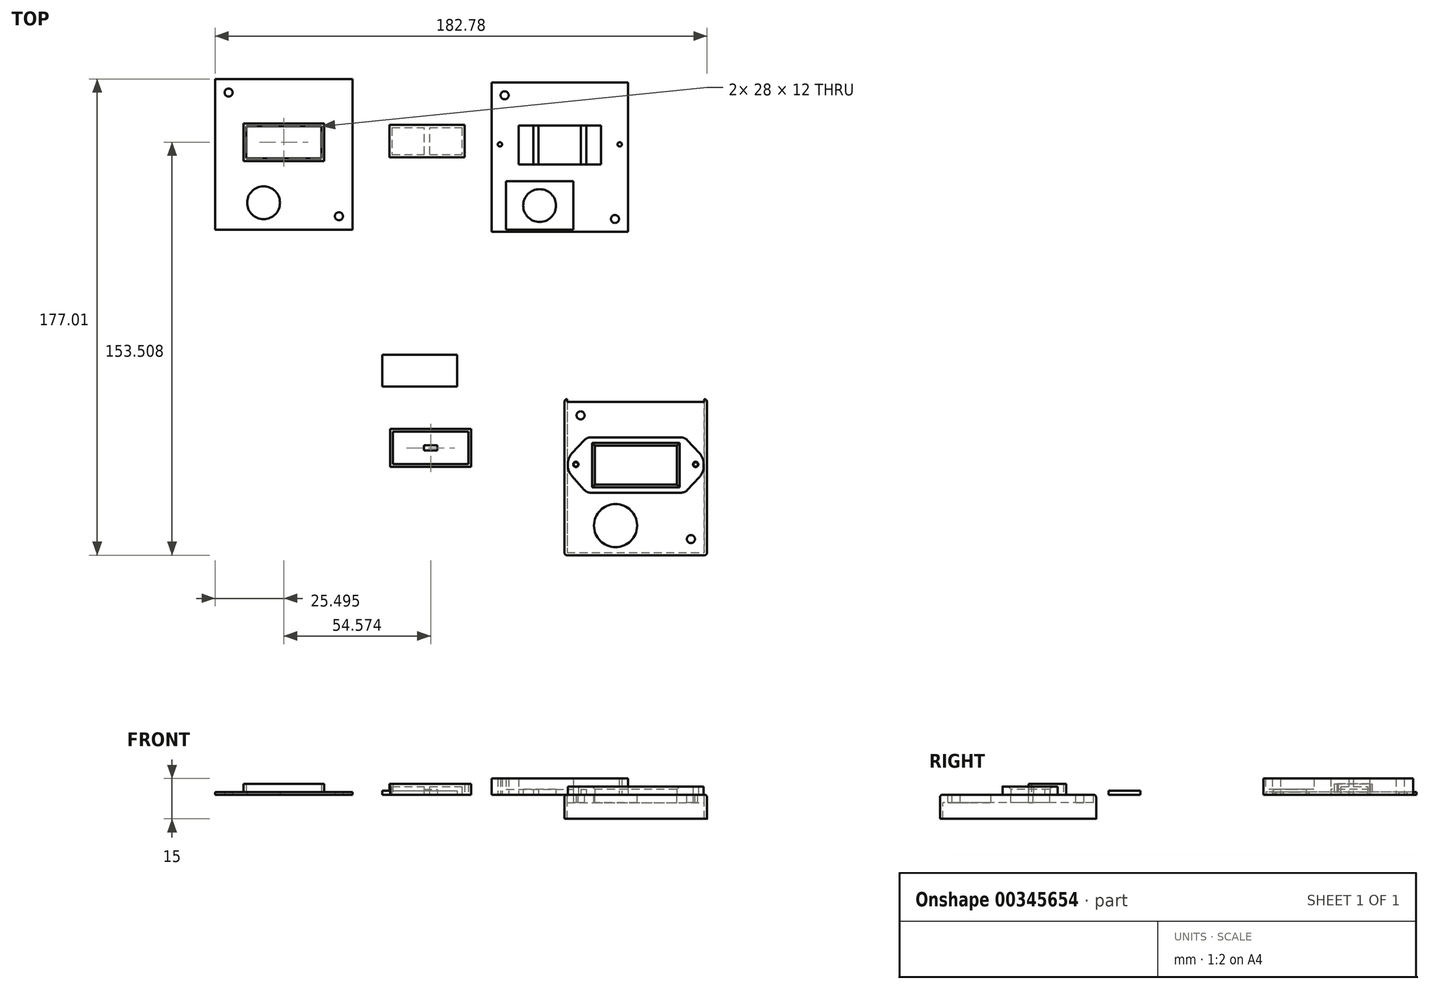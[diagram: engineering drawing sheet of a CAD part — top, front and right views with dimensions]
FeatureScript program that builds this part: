
annotation { "Feature Type Name" : "Feature", "Feature Type Description" : "" }
export const myFeature = defineFeature(function(context is Context, id is Id, definition is map)
    precondition{}
    {
        {
            var Q0;
            Q0=qCreatedBy(makeId("Top.planeOp"),FACE);
            var sketch = newSketch(context, id + "F0", { "sketchPlane" : qUnion([Q0])});
            skLineSegment(sketch, "E0.bottom", {"start": v(25.5, 28) * mm, "end": v(-25.5, 28) * mm});
            skLineSegment(sketch, "E0.top", {"start": v(25.5, -28) * mm, "end": v(-25.5, -28) * mm});
            skLineSegment(sketch, "E0.left", {"start": v(25.5, 28) * mm, "end": v(25.5, -28) * mm});
            skLineSegment(sketch, "E0.right", {"start": v(-25.5, 28) * mm, "end": v(-25.5, -28) * mm});
            skCircle(sketch, "E1", {"center": v(-20.5, 23) * mm, "radius": 1.5 * mm});
            skCircle(sketch, "E2", {"center": v(20.5, -23) * mm, "radius": 1.5 * mm});
            skCircle(sketch, "E3", {"center": v(-7.5, -18) * mm, "radius": 6.1 * mm});
            skLineSegment(sketch, "E4.bottom", {"start": v(-15.25, 11.75) * mm, "end": v(15.25, 11.75) * mm});
            skLineSegment(sketch, "E4.top", {"start": v(-15.25, -2.75) * mm, "end": v(15.25, -2.75) * mm});
            skLineSegment(sketch, "E4.left", {"start": v(-15.25, 11.75) * mm, "end": v(-15.25, -2.75) * mm});
            skLineSegment(sketch, "E4.right", {"start": v(15.25, 11.75) * mm, "end": v(15.25, -2.75) * mm});
            skPoint(sketch, "E5.middle", {"position": v(-103.8, -4.8) * mm});
            skLineSegment(sketch, "E6.bottom", {"start": v(-116.57, 11.54) * mm, "end": v(-88.57, 11.54) * mm});
            skLineSegment(sketch, "E6.top", {"start": v(-116.57, -0.46) * mm, "end": v(-88.57, -0.46) * mm});
            skLineSegment(sketch, "E6.left", {"start": v(-116.57, 11.54) * mm, "end": v(-116.57, -0.46) * mm});
            skLineSegment(sketch, "E6.right", {"start": v(-88.57, 11.54) * mm, "end": v(-88.57, -0.46) * mm});
            skLineSegment(sketch, "E7.bottom", {"start": v(-112.82, 11.54) * mm, "end": v(-110.32, 11.54) * mm});
            skLineSegment(sketch, "E7.top", {"start": v(-112.82, -0.46) * mm, "end": v(-110.32, -0.46) * mm});
            skLineSegment(sketch, "E7.left", {"start": v(-112.82, 11.54) * mm, "end": v(-112.82, -0.46) * mm});
            skLineSegment(sketch, "E7.right", {"start": v(-110.32, 11.54) * mm, "end": v(-110.32, -0.46) * mm});
            skLineSegment(sketch, "E8.bottom", {"start": v(-94.82, 11.54) * mm, "end": v(-92.32, 11.54) * mm});
            skLineSegment(sketch, "E8.top", {"start": v(-94.82, -0.46) * mm, "end": v(-92.32, -0.46) * mm});
            skLineSegment(sketch, "E8.left", {"start": v(-94.82, 11.54) * mm, "end": v(-94.82, -0.46) * mm});
            skLineSegment(sketch, "E8.right", {"start": v(-92.32, 11.54) * mm, "end": v(-92.32, -0.46) * mm});
            skLineSegment(sketch, "E9.bottom", {"start": v(-114.57, 8.54) * mm, "end": v(-108.57, 8.54) * mm, "construction": true});
            skLineSegment(sketch, "E9.top", {"start": v(-114.57, 2.54) * mm, "end": v(-108.57, 2.54) * mm, "construction": true});
            skLineSegment(sketch, "E9.left", {"start": v(-114.57, 8.54) * mm, "end": v(-114.57, 2.54) * mm, "construction": true});
            skLineSegment(sketch, "E9.right", {"start": v(-108.57, 8.54) * mm, "end": v(-108.57, 2.54) * mm, "construction": true});
            skLineSegment(sketch, "E10.bottom", {"start": v(-96.57, 8.54) * mm, "end": v(-90.57, 8.54) * mm, "construction": true});
            skLineSegment(sketch, "E10.top", {"start": v(-96.57, 2.54) * mm, "end": v(-90.57, 2.54) * mm, "construction": true});
            skLineSegment(sketch, "E10.left", {"start": v(-96.57, 8.54) * mm, "end": v(-96.57, 2.54) * mm, "construction": true});
            skLineSegment(sketch, "E10.right", {"start": v(-90.57, 8.54) * mm, "end": v(-90.57, 2.54) * mm, "construction": true});
            skLineSegment(sketch, "E11.bottom", {"start": v(-2.5, 11.75) * mm, "end": v(2.5, 11.75) * mm});
            skLineSegment(sketch, "E11.top", {"start": v(-2.5, -2.75) * mm, "end": v(2.5, -2.75) * mm});
            skLineSegment(sketch, "E11.left", {"start": v(-2.5, 11.75) * mm, "end": v(-2.5, -2.75) * mm});
            skLineSegment(sketch, "E11.right", {"start": v(2.5, 11.75) * mm, "end": v(2.5, -2.75) * mm});
            skLineSegment(sketch, "E12.bottom", {"start": v(-6.25, 10.5) * mm, "end": v(5.75, 10.5) * mm, "construction": true});
            skLineSegment(sketch, "E12.top", {"start": v(-6.25, -1.5) * mm, "end": v(5.75, -1.5) * mm, "construction": true});
            skLineSegment(sketch, "E12.left", {"start": v(-6.25, 10.5) * mm, "end": v(-6.25, -1.5) * mm, "construction": true});
            skLineSegment(sketch, "E12.right", {"start": v(5.75, 10.5) * mm, "end": v(5.75, -1.5) * mm, "construction": true});
            skLineSegment(sketch, "E13.bottom", {"start": v(-128.07, 29.04) * mm, "end": v(-77.07, 29.04) * mm});
            skLineSegment(sketch, "E13.top", {"start": v(-128.07, -26.96) * mm, "end": v(-77.07, -26.96) * mm});
            skLineSegment(sketch, "E13.left", {"start": v(-128.07, 29.04) * mm, "end": v(-128.07, -26.96) * mm});
            skLineSegment(sketch, "E13.right", {"start": v(-77.07, 29.04) * mm, "end": v(-77.07, -26.96) * mm});
            skCircle(sketch, "E14", {"center": v(-123.07, 24.04) * mm, "radius": 1.5 * mm});
            skCircle(sketch, "E15", {"center": v(-82.07, -21.96) * mm, "radius": 1.5 * mm});
            skLineSegment(sketch, "E16.bottom", {"start": v(-14, 10.5) * mm, "end": v(14, 10.5) * mm, "construction": true});
            skLineSegment(sketch, "E16.top", {"start": v(-14, -1.5) * mm, "end": v(14, -1.5) * mm, "construction": true});
            skLineSegment(sketch, "E16.left", {"start": v(-14, 10.5) * mm, "end": v(-14, -1.5) * mm, "construction": true});
            skLineSegment(sketch, "E16.right", {"start": v(14, 10.5) * mm, "end": v(14, -1.5) * mm, "construction": true});
            skCircle(sketch, "E17", {"center": v(-110.07, -16.96) * mm, "radius": 6.1 * mm});
            skSolve(sketch);
        }
        {
            var Q0;
            Q0=makeQuery(id+"F0.imprint","IMPRINT",FACE,{"disambiguationData":[TD([[makeQuery(id+"F0.imprint","IMPRINT",EDGE,{"derivedFrom":sQuery(id+"F0.wireOp",EDGE,"E0.bottom")}),1.0]])]});
            var Q1;
            Q1=makeQuery(id+"F0.imprint","IMPRINT",FACE,{"disambiguationData":[TD([[makeQuery(id+"F0.imprint","IMPRINT",EDGE,{"derivedFrom":sQuery(id+"F0.wireOp",EDGE,"LN2d2Qam-zQ4N-hJWI-jsZm-hQ2YjQqxJFMe.bottom")}),-1.0]])]});
            var Q2;
            Q2=makeQuery(id+"F0.imprint","IMPRINT",FACE,{"disambiguationData":[TD([[makeQuery(id+"F0.imprint","IMPRINT",EDGE,{"derivedFrom":sQuery(id+"F0.wireOp",EDGE,"Tyq8l7xN-NJ6r-rAiC-5Q4v-MCzvgNdMf9WX.bottom")}),-1.0]])]});
            var Q3;
            Q3=makeQuery(id+"F0.imprint","IMPRINT",FACE,{"disambiguationData":[TD([[makeQuery(id+"F0.imprint","IMPRINT",EDGE,{"derivedFrom":sQuery(id+"F0.wireOp",EDGE,"E11.bottom")}),-1.0]])]});
            var Q4;
            {var subQ12=sQuery(id+"F0.wireOp",EDGE,"E6.left");Q4=makeQuery(id+"F0.imprint","IMPRINT",FACE,{"disambiguationData":[TD([[makeQuery(id+"F0.imprint","IMPRINT",EDGE,{"derivedFrom":subQ12}),-1.0]])]});}
            var Q5;
            Q5=makeQuery(id+"F0.imprint","IMPRINT",FACE,{"disambiguationData":[TD([[makeQuery(id+"F0.imprint","IMPRINT",EDGE,{"derivedFrom":sQuery(id+"F0.wireOp",EDGE,"E7.bottom")}),-1.0]])]});
            var Q6;
            Q6=makeQuery(id+"F0.imprint","IMPRINT",FACE,{"disambiguationData":[TD([[makeQuery(id+"F0.imprint","IMPRINT",EDGE,{"derivedFrom":sQuery(id+"F0.wireOp",EDGE,"E8.bottom")}),-1.0]])]});
            var Q7;
            Q7=makeQuery(id+"F0.imprint","IMPRINT",FACE,{"disambiguationData":[TD([[makeQuery(id+"F0.imprint","IMPRINT",EDGE,{"derivedFrom":sQuery(id+"F0.wireOp",EDGE,"V3zyF6Pa-9TGi-MSfi-dUwD-Oto6uP0OLka4.bottom")}),-1.0]])]});
            extrude(context, id + "F1", {"entities" : qUnion([Q0, Q1, Q2, Q3, Q4, Q5, Q6, Q7]), "depth" : 1 * mm});
        }
        {
            var Q0;
            Q0=qCreatedBy(makeId("Top.planeOp"),FACE);
            var sketch = newSketch(context, id + "F2", { "sketchPlane" : qUnion([Q0])});
            skPoint(sketch, "E18.middle", {"position": v(28.78, -122.02) * mm});
            skLineSegment(sketch, "E19.bottom", {"start": v(14.21, -108.47) * mm, "end": v(42.21, -108.47) * mm, "construction": true});
            skLineSegment(sketch, "E19.top", {"start": v(14.21, -120.47) * mm, "end": v(42.21, -120.47) * mm, "construction": true});
            skLineSegment(sketch, "E19.left", {"start": v(14.21, -108.47) * mm, "end": v(14.21, -120.47) * mm, "construction": true});
            skLineSegment(sketch, "E19.right", {"start": v(42.21, -108.47) * mm, "end": v(42.21, -120.47) * mm, "construction": true});
            skLineSegment(sketch, "E20.bottom", {"start": v(20.96, -108.47) * mm, "end": v(23.46, -108.47) * mm, "construction": true});
            skLineSegment(sketch, "E20.top", {"start": v(20.96, -120.47) * mm, "end": v(23.46, -120.47) * mm, "construction": true});
            skLineSegment(sketch, "E20.left", {"start": v(20.96, -108.47) * mm, "end": v(20.96, -120.47) * mm, "construction": true});
            skLineSegment(sketch, "E20.right", {"start": v(23.46, -108.47) * mm, "end": v(23.46, -120.47) * mm, "construction": true});
            skLineSegment(sketch, "E21.bottom", {"start": v(32.96, -108.47) * mm, "end": v(35.46, -108.47) * mm, "construction": true});
            skLineSegment(sketch, "E21.top", {"start": v(32.96, -120.47) * mm, "end": v(35.46, -120.47) * mm, "construction": true});
            skLineSegment(sketch, "E21.left", {"start": v(32.96, -108.47) * mm, "end": v(32.96, -120.47) * mm, "construction": true});
            skLineSegment(sketch, "E21.right", {"start": v(35.46, -108.47) * mm, "end": v(35.46, -120.47) * mm, "construction": true});
            skLineSegment(sketch, "E22.bottom", {"start": v(19.21, -111.47) * mm, "end": v(25.21, -111.47) * mm, "construction": true});
            skLineSegment(sketch, "E22.top", {"start": v(19.21, -117.47) * mm, "end": v(25.21, -117.47) * mm, "construction": true});
            skLineSegment(sketch, "E22.left", {"start": v(19.21, -111.47) * mm, "end": v(19.21, -117.47) * mm, "construction": true});
            skLineSegment(sketch, "E22.right", {"start": v(25.21, -111.47) * mm, "end": v(25.21, -117.47) * mm, "construction": true});
            skLineSegment(sketch, "E23.bottom", {"start": v(31.21, -111.47) * mm, "end": v(37.21, -111.47) * mm, "construction": true});
            skLineSegment(sketch, "E23.top", {"start": v(31.21, -117.47) * mm, "end": v(37.21, -117.47) * mm, "construction": true});
            skLineSegment(sketch, "E23.left", {"start": v(31.21, -111.47) * mm, "end": v(31.21, -117.47) * mm, "construction": true});
            skLineSegment(sketch, "E23.right", {"start": v(37.21, -111.47) * mm, "end": v(37.21, -117.47) * mm, "construction": true});
            skLineSegment(sketch, "E24.bottom", {"start": v(2.71, -90.97) * mm, "end": v(53.71, -90.97) * mm});
            skLineSegment(sketch, "E24.top", {"start": v(2.71, -146.97) * mm, "end": v(53.71, -146.97) * mm});
            skLineSegment(sketch, "E24.left", {"start": v(2.71, -90.97) * mm, "end": v(2.71, -146.97) * mm});
            skLineSegment(sketch, "E24.right", {"start": v(53.71, -90.97) * mm, "end": v(53.71, -146.97) * mm});
            skCircle(sketch, "E25", {"center": v(7.71, -95.97) * mm, "radius": 1.5 * mm});
            skCircle(sketch, "E26", {"center": v(48.71, -141.97) * mm, "radius": 1.5 * mm});
            skCircle(sketch, "E27", {"center": v(20.71, -136.97) * mm, "radius": 8 * mm});
            skLineSegment(sketch, "E28.bottom", {"start": v(12.96, -107.22) * mm, "end": v(43.46, -107.22) * mm});
            skLineSegment(sketch, "E28.top", {"start": v(12.96, -121.72) * mm, "end": v(43.46, -121.72) * mm});
            skLineSegment(sketch, "E28.left", {"start": v(12.96, -107.22) * mm, "end": v(12.96, -121.72) * mm});
            skLineSegment(sketch, "E28.right", {"start": v(43.46, -107.22) * mm, "end": v(43.46, -121.72) * mm});
            skPoint(sketch, "E29.middle", {"position": v(-49.22, -118.43) * mm});
            skLineSegment(sketch, "E30.bottom", {"start": v(-62, -102.08) * mm, "end": v(-34, -102.08) * mm});
            skLineSegment(sketch, "E30.top", {"start": v(-62, -114.08) * mm, "end": v(-34, -114.08) * mm});
            skLineSegment(sketch, "E30.left", {"start": v(-62, -102.08) * mm, "end": v(-62, -114.08) * mm});
            skLineSegment(sketch, "E30.right", {"start": v(-34, -102.08) * mm, "end": v(-34, -114.08) * mm});
            skLineSegment(sketch, "E31.bottom", {"start": v(-54.75, -102.08) * mm, "end": v(-52.25, -102.08) * mm, "construction": true});
            skLineSegment(sketch, "E31.top", {"start": v(-54.75, -114.08) * mm, "end": v(-52.25, -114.08) * mm, "construction": true});
            skLineSegment(sketch, "E31.left", {"start": v(-54.75, -102.08) * mm, "end": v(-54.75, -114.08) * mm, "construction": true});
            skLineSegment(sketch, "E31.right", {"start": v(-52.25, -102.08) * mm, "end": v(-52.25, -114.08) * mm, "construction": true});
            skLineSegment(sketch, "E32.bottom", {"start": v(-43.75, -102.08) * mm, "end": v(-41.25, -102.08) * mm, "construction": true});
            skLineSegment(sketch, "E32.top", {"start": v(-43.75, -114.08) * mm, "end": v(-41.25, -114.08) * mm, "construction": true});
            skLineSegment(sketch, "E32.left", {"start": v(-43.75, -102.08) * mm, "end": v(-43.75, -114.08) * mm, "construction": true});
            skLineSegment(sketch, "E32.right", {"start": v(-41.25, -102.08) * mm, "end": v(-41.25, -114.08) * mm, "construction": true});
            skLineSegment(sketch, "E33.bottom", {"start": v(-56.5, -105.08) * mm, "end": v(-50.5, -105.08) * mm, "construction": true});
            skLineSegment(sketch, "E33.top", {"start": v(-56.5, -111.08) * mm, "end": v(-50.5, -111.08) * mm, "construction": true});
            skLineSegment(sketch, "E33.left", {"start": v(-56.5, -105.08) * mm, "end": v(-56.5, -111.08) * mm, "construction": true});
            skLineSegment(sketch, "E33.right", {"start": v(-50.5, -105.08) * mm, "end": v(-50.5, -111.08) * mm, "construction": true});
            skLineSegment(sketch, "E34.bottom", {"start": v(-45.5, -105.08) * mm, "end": v(-39.5, -105.08) * mm, "construction": true});
            skLineSegment(sketch, "E34.top", {"start": v(-45.5, -111.08) * mm, "end": v(-39.5, -111.08) * mm, "construction": true});
            skLineSegment(sketch, "E34.left", {"start": v(-45.5, -105.08) * mm, "end": v(-45.5, -111.08) * mm, "construction": true});
            skLineSegment(sketch, "E34.right", {"start": v(-39.5, -105.08) * mm, "end": v(-39.5, -111.08) * mm, "construction": true});
            skLineSegment(sketch, "E35.bottom", {"start": v(-63, -101.08) * mm, "end": v(-33, -101.08) * mm});
            skLineSegment(sketch, "E35.top", {"start": v(-63, -115.08) * mm, "end": v(-33, -115.08) * mm});
            skLineSegment(sketch, "E35.left", {"start": v(-63, -101.08) * mm, "end": v(-63, -115.08) * mm});
            skLineSegment(sketch, "E35.right", {"start": v(-33, -101.08) * mm, "end": v(-33, -115.08) * mm});
            skLineSegment(sketch, "E36.bottom", {"start": v(-50.5, -107.08) * mm, "end": v(-45.5, -107.08) * mm});
            skLineSegment(sketch, "E36.right", {"start": v(-34, -107.08) * mm, "end": v(-34, -109.08) * mm});
            skLineSegment(sketch, "E37.bottom", {"start": v(-50.5, -102.08) * mm, "end": v(-45.5, -102.08) * mm});
            skLineSegment(sketch, "E37.top", {"start": v(-50.5, -114.08) * mm, "end": v(-45.5, -114.08) * mm});
            skLineSegment(sketch, "E37.left", {"start": v(-50.5, -102.08) * mm, "end": v(-50.5, -114.08) * mm});
            skLineSegment(sketch, "E37.right", {"start": v(-45.5, -102.08) * mm, "end": v(-45.5, -114.08) * mm});
            skLineSegment(sketch, "E38.top", {"start": v(2.71, -89.97) * mm, "end": v(53.71, -89.97) * mm});
            skLineSegment(sketch, "E38.left", {"start": v(2.71, -90.97) * mm, "end": v(2.71, -89.97) * mm});
            skLineSegment(sketch, "E38.right", {"start": v(53.71, -90.97) * mm, "end": v(53.71, -89.97) * mm});
            skLineSegment(sketch, "E39.top", {"start": v(2.71, -147.97) * mm, "end": v(53.71, -147.97) * mm});
            skLineSegment(sketch, "E39.left", {"start": v(2.71, -146.97) * mm, "end": v(2.71, -147.97) * mm});
            skLineSegment(sketch, "E39.right", {"start": v(53.71, -146.97) * mm, "end": v(53.71, -147.97) * mm});
            skLineSegment(sketch, "E40.bottom", {"start": v(53.71, -89.97) * mm, "end": v(54.71, -89.97) * mm});
            skLineSegment(sketch, "E40.top", {"start": v(53.71, -147.97) * mm, "end": v(54.71, -147.97) * mm});
            skLineSegment(sketch, "E40.left", {"start": v(53.71, -89.97) * mm, "end": v(53.71, -147.97) * mm});
            skLineSegment(sketch, "E40.right", {"start": v(54.71, -89.97) * mm, "end": v(54.71, -147.97) * mm});
            skLineSegment(sketch, "E41.bottom", {"start": v(2.71, -89.97) * mm, "end": v(1.71, -89.97) * mm});
            skLineSegment(sketch, "E41.top", {"start": v(2.71, -147.97) * mm, "end": v(1.71, -147.97) * mm});
            skLineSegment(sketch, "E41.left", {"start": v(2.71, -89.97) * mm, "end": v(2.71, -147.97) * mm});
            skLineSegment(sketch, "E41.right", {"start": v(1.71, -89.97) * mm, "end": v(1.71, -147.97) * mm});
            skCircle(sketch, "E42", {"center": v(5.96, -114.22) * mm, "radius": 0.8 * mm});
            skCircle(sketch, "E43", {"center": v(50.46, -114.22) * mm, "radius": 0.8 * mm});
            skLineSegment(sketch, "E44.trimOffspring", {"start": v(-50.5, -109.08) * mm, "end": v(-45.5, -109.08) * mm});
            skSolve(sketch);
        }
        {
            var Q0;
            Q0=makeQuery(id+"F1.opExtrude","CAP_FACE",FACE,{"disambiguationData":[OSD([sQuery(id+"F0.wireOp",EDGE,"E6.bottom"),sQuery(id+"F0.wireOp",EDGE,"E6.top"),sQuery(id+"F0.wireOp",EDGE,"E6.left"),sQuery(id+"F0.wireOp",EDGE,"E6.right"),sQuery(id+"F0.wireOp",EDGE,"E7.left"),sQuery(id+"F0.wireOp",EDGE,"E7.right"),sQuery(id+"F0.wireOp",EDGE,"E8.left"),sQuery(id+"F0.wireOp",EDGE,"E8.right"),sQuery(id+"F0.wireOp",EDGE,"E13.bottom"),sQuery(id+"F0.wireOp",EDGE,"E13.top"),sQuery(id+"F0.wireOp",EDGE,"E13.left"),sQuery(id+"F0.wireOp",EDGE,"E13.right"),sQuery(id+"F0.wireOp",EDGE,"E14"),sQuery(id+"F0.wireOp",EDGE,"E15"),sQuery(id+"F0.wireOp",EDGE,"E17"),sQuery(id+"F0.wireOp",EDGE,"V3zyF6Pa-9TGi-MSfi-dUwD-Oto6uP0OLka4.left"),sQuery(id+"F0.wireOp",EDGE,"V3zyF6Pa-9TGi-MSfi-dUwD-Oto6uP0OLka4.right")])],"isStart":false});
            var sketch = newSketch(context, id + "F3", { "sketchPlane" : qUnion([Q0])});
            skLineSegment(sketch, "E45.bottom", {"start": v(-116.57, 11.54) * mm, "end": v(-88.57, 11.54) * mm});
            skLineSegment(sketch, "E45.top", {"start": v(-116.57, 12.54) * mm, "end": v(-88.57, 12.54) * mm});
            skLineSegment(sketch, "E45.left", {"start": v(-116.57, 11.54) * mm, "end": v(-116.57, 12.54) * mm});
            skLineSegment(sketch, "E45.right", {"start": v(-88.57, 11.54) * mm, "end": v(-88.57, 12.54) * mm});
            skLineSegment(sketch, "E46.bottom", {"start": v(-116.57, -0.46) * mm, "end": v(-88.57, -0.46) * mm});
            skLineSegment(sketch, "E46.top", {"start": v(-116.57, -1.46) * mm, "end": v(-88.57, -1.46) * mm});
            skLineSegment(sketch, "E46.left", {"start": v(-116.57, -0.46) * mm, "end": v(-116.57, -1.46) * mm});
            skLineSegment(sketch, "E46.right", {"start": v(-88.57, -0.46) * mm, "end": v(-88.57, -1.46) * mm});
            skLineSegment(sketch, "E47.bottom", {"start": v(-116.57, -1.46) * mm, "end": v(-117.57, -1.46) * mm});
            skLineSegment(sketch, "E47.top", {"start": v(-116.57, 12.54) * mm, "end": v(-117.57, 12.54) * mm});
            skLineSegment(sketch, "E47.left", {"start": v(-116.57, -1.46) * mm, "end": v(-116.57, 12.54) * mm});
            skLineSegment(sketch, "E47.right", {"start": v(-117.57, -1.46) * mm, "end": v(-117.57, 12.54) * mm});
            skLineSegment(sketch, "E48.bottom", {"start": v(-88.57, 12.54) * mm, "end": v(-87.57, 12.54) * mm});
            skLineSegment(sketch, "E48.top", {"start": v(-88.57, -1.46) * mm, "end": v(-87.57, -1.46) * mm});
            skLineSegment(sketch, "E48.left", {"start": v(-88.57, 12.54) * mm, "end": v(-88.57, -1.46) * mm});
            skLineSegment(sketch, "E48.right", {"start": v(-87.57, 12.54) * mm, "end": v(-87.57, -1.46) * mm});
            skSolve(sketch);
        }
        {
            var Q0;
            Q0=qSketchRegion(id+"F3",true);
            extrude(context, id + "F4", {"entities" : qUnion([Q0]), "operationType" : NewBodyOperationType.ADD, "depth" : 3 * mm});
        }
        {
            var Q0;
            Q0=qCreatedBy(makeId("Top.planeOp"),FACE);
            var sketch = newSketch(context, id + "F5", { "sketchPlane" : qUnion([Q0])});
            skLineSegment(sketch, "E49.bottom", {"start": v(-63.36, 12) * mm, "end": v(-35.36, 12) * mm});
            skLineSegment(sketch, "E49.top", {"start": v(-63.36, 0) * mm, "end": v(-35.36, 0) * mm});
            skLineSegment(sketch, "E49.left", {"start": v(-63.36, 12) * mm, "end": v(-63.36, 0) * mm});
            skLineSegment(sketch, "E49.right", {"start": v(-35.36, 12) * mm, "end": v(-35.36, 0) * mm});
            skLineSegment(sketch, "E50.bottom", {"start": v(-65.94, -73.47) * mm, "end": v(-38.14, -73.47) * mm});
            skLineSegment(sketch, "E50.top", {"start": v(-65.94, -85.27) * mm, "end": v(-38.14, -85.27) * mm});
            skLineSegment(sketch, "E50.left", {"start": v(-65.94, -73.47) * mm, "end": v(-65.94, -85.27) * mm});
            skLineSegment(sketch, "E50.right", {"start": v(-38.14, -73.47) * mm, "end": v(-38.14, -85.27) * mm});
            skSolve(sketch);
        }
        {
            var Q0;
            Q0=makeQuery(id+"F5.imprint","IMPRINT",FACE,{"disambiguationData":[TD([[makeQuery(id+"F5.imprint","IMPRINT",EDGE,{"derivedFrom":sQuery(id+"F5.wireOp",EDGE,"E49.bottom")}),-1.0]])]});
            extrude(context, id + "F6", {"entities" : qUnion([Q0]), "depth" : 4 * mm});
        }
        {
            var Q0;
            Q0=makeQuery(id+"F6.opExtrude","CAP_FACE",FACE,{"disambiguationData":[OSD([sQuery(id+"F5.wireOp",EDGE,"E49.bottom"),sQuery(id+"F5.wireOp",EDGE,"E49.top"),sQuery(id+"F5.wireOp",EDGE,"E49.left"),sQuery(id+"F5.wireOp",EDGE,"E49.right")])],"isStart":true});
            shell(context, id + "F7", {"entities" : qUnion([Q0]), "thickness" : 1 * mm});
        }
        {
            var Q0;
            Q0=makeQuery(id+"F7.opShell","OFFSET_FACE",FACE,{"disambiguationData":[OSD([sQuery(id+"F5.wireOp",EDGE,"E49.bottom"),sQuery(id+"F5.wireOp",EDGE,"E49.top"),sQuery(id+"F5.wireOp",EDGE,"E49.left"),sQuery(id+"F5.wireOp",EDGE,"E49.right")])]});
            var sketch = newSketch(context, id + "F8", { "sketchPlane" : qUnion([Q0])});
            skLineSegment(sketch, "E51.bottom", {"start": v(-50.36, -1) * mm, "end": v(-48.36, -1) * mm});
            skLineSegment(sketch, "E51.top", {"start": v(-50.36, -11) * mm, "end": v(-48.36, -11) * mm});
            skLineSegment(sketch, "E51.left", {"start": v(-50.36, -1) * mm, "end": v(-50.36, -11) * mm});
            skLineSegment(sketch, "E51.right", {"start": v(-48.36, -1) * mm, "end": v(-48.36, -11) * mm});
            skSolve(sketch);
        }
        {
            var Q0;
            Q0=makeQuery(id+"F8.imprint","IMPRINT",FACE,{"disambiguationData":[TD([[makeQuery(id+"F8.imprint","IMPRINT",EDGE,{"derivedFrom":sQuery(id+"F8.wireOp",EDGE,"E51.bottom")}),-1.0]])]});
            extrude(context, id + "F9", {"entities" : qUnion([Q0]), "operationType" : NewBodyOperationType.ADD, "depth" : 3 * mm});
        }
        {
            var Q0;
            Q0=makeQuery(id+"F1.opExtrude","CAP_FACE",FACE,{"disambiguationData":[OSD([sQuery(id+"F0.wireOp",EDGE,"E0.bottom"),sQuery(id+"F0.wireOp",EDGE,"E0.top"),sQuery(id+"F0.wireOp",EDGE,"E0.left"),sQuery(id+"F0.wireOp",EDGE,"E0.right"),sQuery(id+"F0.wireOp",EDGE,"E1"),sQuery(id+"F0.wireOp",EDGE,"E2"),sQuery(id+"F0.wireOp",EDGE,"E3"),sQuery(id+"F0.wireOp",EDGE,"E4.bottom"),sQuery(id+"F0.wireOp",EDGE,"E4.top"),sQuery(id+"F0.wireOp",EDGE,"E4.left"),sQuery(id+"F0.wireOp",EDGE,"E4.right"),sQuery(id+"F0.wireOp",EDGE,"E11.left"),sQuery(id+"F0.wireOp",EDGE,"E11.right")])],"isStart":false});
            var sketch = newSketch(context, id + "F10", { "sketchPlane" : qUnion([Q0])});
            skLineSegment(sketch, "E52.bottom", {"start": v(-6.25, 10.25) * mm, "end": v(5.75, 10.25) * mm, "construction": true});
            skLineSegment(sketch, "E52.top", {"start": v(-6.25, -1.75) * mm, "end": v(5.75, -1.75) * mm, "construction": true});
            skLineSegment(sketch, "E52.left", {"start": v(-6.25, 10.25) * mm, "end": v(-6.25, -1.75) * mm, "construction": true});
            skLineSegment(sketch, "E52.right", {"start": v(5.75, 10.25) * mm, "end": v(5.75, -1.75) * mm, "construction": true});
            skSolve(sketch);
        }
        {
            var Q0;
            {var subQ3=sQuery(id+"F2.wireOp",EDGE,"E30.left");Q0=makeQuery(id+"F2.imprint","IMPRINT",FACE,{"disambiguationData":[TD([[makeQuery(id+"F2.imprint","IMPRINT",EDGE,{"derivedFrom":subQ3}),-1.0]])]});}
            extrude(context, id + "F11", {"entities" : qUnion([Q0]), "depth" : 4 * mm});
        }
        {
            var Q0;
            Q0=makeQuery(id+"F2.imprint","IMPRINT",FACE,{"disambiguationData":[TD([[makeQuery(id+"F2.imprint","IMPRINT",EDGE,{"derivedFrom":sQuery(id+"F2.wireOp",EDGE,"E25")}),-1.0]])]});
            extrude(context, id + "F12", {"entities" : qUnion([Q0]), "oppositeDirection" : true, "depth" : 3 * mm});
        }
        {
            var Q0;
            Q0=makeQuery(id+"F2.imprint","IMPRINT",FACE,{"disambiguationData":[TD([[makeQuery(id+"F2.imprint","IMPRINT",EDGE,{"derivedFrom":sQuery(id+"F2.wireOp",EDGE,"E36.bottom")}),-1.0]])]});
            var Q1;
            {var subQ5=sQuery(id+"F2.wireOp",EDGE,"E37.bottom");Q1=makeQuery(id+"F2.imprint","IMPRINT",FACE,{"disambiguationData":[TD([[makeQuery(id+"F2.imprint","IMPRINT",EDGE,{"derivedFrom":subQ5}),-1.0]])]});}
            var Q2;
            {var subQ5=sQuery(id+"F2.wireOp",EDGE,"E37.top");Q2=makeQuery(id+"F2.imprint","IMPRINT",FACE,{"disambiguationData":[TD([[makeQuery(id+"F2.imprint","IMPRINT",EDGE,{"derivedFrom":subQ5}),1.0]])]});}
            extrude(context, id + "F13", {"entities" : qUnion([Q0, Q1, Q2]), "operationType" : NewBodyOperationType.ADD, "depth" : 2 * mm});
        }
        {
            var Q0;
            Q0=makeQuery(id+"F5.imprint","IMPRINT",FACE,{"disambiguationData":[TD([[makeQuery(id+"F5.imprint","IMPRINT",EDGE,{"derivedFrom":sQuery(id+"F5.wireOp",EDGE,"E50.bottom")}),-1.0]])]});
            extrude(context, id + "F14", {"entities" : qUnion([Q0]), "depth" : 1.5 * mm});
        }
        {
            var Q0;
            {var subQ3=sQuery(id+"F2.wireOp",EDGE,"E41.bottom");Q0=makeQuery(id+"F2.imprint","IMPRINT",FACE,{"disambiguationData":[TD([[makeQuery(id+"F2.imprint","IMPRINT",EDGE,{"derivedFrom":subQ3}),1.0]])]});}
            var Q1;
            {var subQ0=sQuery(id+"F2.wireOp",EDGE,"E24.bottom");Q1=makeQuery(id+"F2.imprint","IMPRINT",FACE,{"disambiguationData":[TD([[makeQuery(id+"F2.imprint","IMPRINT",EDGE,{"derivedFrom":subQ0}),1.0]])]});}
            var Q2;
            {var subQ0=sQuery(id+"F2.wireOp",EDGE,"E24.top");Q2=makeQuery(id+"F2.imprint","IMPRINT",FACE,{"disambiguationData":[TD([[makeQuery(id+"F2.imprint","IMPRINT",EDGE,{"derivedFrom":subQ0}),-1.0]])]});}
            var Q3;
            {var subQ3=sQuery(id+"F2.wireOp",EDGE,"E40.bottom");Q3=makeQuery(id+"F2.imprint","IMPRINT",FACE,{"disambiguationData":[TD([[makeQuery(id+"F2.imprint","IMPRINT",EDGE,{"derivedFrom":subQ3}),-1.0]])]});}
            extrude(context, id + "F15", {"entities" : qUnion([Q0, Q1, Q2, Q3]), "operationType" : NewBodyOperationType.ADD, "oppositeDirection" : true, "depth" : 9 * mm});
        }
        {
            var Q0;
            Q0=makeQuery(id+"F2.imprint","IMPRINT",FACE,{"disambiguationData":[TD([[makeQuery(id+"F2.imprint","IMPRINT",EDGE,{"derivedFrom":sQuery(id+"F2.wireOp",EDGE,"E25")}),-1.0]])]});
            var sketch = newSketch(context, id + "F16", { "sketchPlane" : qUnion([Q0])});
            skLineSegment(sketch, "E53.bottom", {"start": v(9.96, -104.22) * mm, "end": v(46.46, -104.22) * mm});
            skLineSegment(sketch, "E53.top", {"start": v(9.96, -124.72) * mm, "end": v(46.46, -124.72) * mm});
            skLineSegment(sketch, "E53.left", {"start": v(9.96, -104.22) * mm, "end": v(9.96, -124.72) * mm});
            skLineSegment(sketch, "E53.right", {"start": v(46.46, -104.22) * mm, "end": v(46.46, -124.72) * mm});
            skLineSegment(sketch, "E54", {"start": v(9.96, -124.72) * mm, "end": v(2.96, -116.72) * mm});
            skLineSegment(sketch, "E55", {"start": v(2.96, -116.72) * mm, "end": v(2.96, -111.72) * mm});
            skLineSegment(sketch, "E56", {"start": v(2.96, -111.72) * mm, "end": v(9.96, -104.22) * mm});
            skCircle(sketch, "E57", {"center": v(5.96, -114.22) * mm, "radius": 1 * mm});
            skLineSegment(sketch, "E58.bottom", {"start": v(12.96, -107.22) * mm, "end": v(43.46, -107.22) * mm});
            skLineSegment(sketch, "E58.top", {"start": v(12.96, -121.72) * mm, "end": v(43.46, -121.72) * mm});
            skLineSegment(sketch, "E58.left", {"start": v(12.96, -107.22) * mm, "end": v(12.96, -121.72) * mm});
            skLineSegment(sketch, "E58.right", {"start": v(43.46, -107.22) * mm, "end": v(43.46, -121.72) * mm});
            skLineSegment(sketch, "E59", {"start": v(46.46, -104.22) * mm, "end": v(53.46, -111.72) * mm});
            skLineSegment(sketch, "E60", {"start": v(53.46, -111.72) * mm, "end": v(53.46, -117.22) * mm});
            skLineSegment(sketch, "E61", {"start": v(53.46, -117.22) * mm, "end": v(46.46, -124.72) * mm});
            skCircle(sketch, "E62", {"center": v(50.46, -114.22) * mm, "radius": 1 * mm});
            skSolve(sketch);
        }
        {
            var Q0;
            Q0=qSketchRegion(id+"F16",true);
            extrude(context, id + "F17", {"entities" : qUnion([Q0]), "depth" : 3 * mm});
        }
        {
            var Q0;
            Q0=makeQuery(id+"F17.opExtrude","SWEPT_EDGE",EDGE,{"disambiguationData":[OSD([sQuery(id+"F16.wireOp",EDGE,"E55"),sQuery(id+"F16.wireOp",EDGE,"E56")])]});
            var Q1;
            Q1=makeQuery(id+"F17.opExtrude","SWEPT_EDGE",EDGE,{"disambiguationData":[OSD([sQuery(id+"F16.wireOp",EDGE,"E54"),sQuery(id+"F16.wireOp",EDGE,"E55")])]});
            var Q2;
            Q2=makeQuery(id+"F17.opExtrude","SWEPT_EDGE",EDGE,{"disambiguationData":[OSD([sQuery(id+"F16.wireOp",EDGE,"E60"),sQuery(id+"F16.wireOp",EDGE,"E61")])]});
            var Q3;
            Q3=makeQuery(id+"F17.opExtrude","SWEPT_EDGE",EDGE,{"disambiguationData":[OSD([sQuery(id+"F16.wireOp",EDGE,"E59"),sQuery(id+"F16.wireOp",EDGE,"E60")])]});
            fillet(context, id + "F18", {"entities" : qUnion([Q0, Q1, Q2, Q3]), "radius" : 6 * mm, "tangentPropagation" : true, "allowEdgeOverflow" : false});
        }
        {
            var Q0;
            Q0=makeQuery(id+"F17.opExtrude","SWEPT_EDGE",EDGE,{"disambiguationData":[OSD([sQuery(id+"F16.wireOp",EDGE,"E53.bottom"),sQuery(id+"F16.wireOp",EDGE,"E53.left"),sQuery(id+"F16.wireOp",EDGE,"E56")])]});
            var Q1;
            Q1=makeQuery(id+"F17.opExtrude","SWEPT_EDGE",EDGE,{"disambiguationData":[OSD([sQuery(id+"F16.wireOp",EDGE,"E53.top"),sQuery(id+"F16.wireOp",EDGE,"E53.left"),sQuery(id+"F16.wireOp",EDGE,"E54")])]});
            var Q2;
            Q2=makeQuery(id+"F17.opExtrude","SWEPT_EDGE",EDGE,{"disambiguationData":[OSD([sQuery(id+"F16.wireOp",EDGE,"E53.top"),sQuery(id+"F16.wireOp",EDGE,"E53.right"),sQuery(id+"F16.wireOp",EDGE,"E61")])]});
            var Q3;
            Q3=makeQuery(id+"F17.opExtrude","SWEPT_EDGE",EDGE,{"disambiguationData":[OSD([sQuery(id+"F16.wireOp",EDGE,"E53.bottom"),sQuery(id+"F16.wireOp",EDGE,"E53.right"),sQuery(id+"F16.wireOp",EDGE,"E59")])]});
            fillet(context, id + "F19", {"entities" : qUnion([Q0, Q1, Q2, Q3]), "radius" : 3 * mm, "tangentPropagation" : true, "allowEdgeOverflow" : false});
        }
        {
            var Q0;
            Q0=makeQuery(id+"F15.opExtrude","CAP_EDGE",EDGE,{"disambiguationData":[OSD([sQuery(id+"F2.wireOp",EDGE,"E41.right")])],"isStart":true});
            var Q1;
            Q1=makeQuery(id+"F15.opExtrude","CAP_EDGE",EDGE,{"disambiguationData":[OSD([sQuery(id+"F2.wireOp",EDGE,"E38.top"),sQuery(id+"F2.wireOp",EDGE,"E40.bottom"),sQuery(id+"F2.wireOp",EDGE,"E41.bottom")])],"isStart":true});
            var Q2;
            Q2=makeQuery(id+"F15.opExtrude","CAP_EDGE",EDGE,{"disambiguationData":[OSD([sQuery(id+"F2.wireOp",EDGE,"E39.top"),sQuery(id+"F2.wireOp",EDGE,"E40.top"),sQuery(id+"F2.wireOp",EDGE,"E41.top")])],"isStart":true});
            var Q3;
            Q3=makeQuery(id+"F15.opExtrude","CAP_EDGE",EDGE,{"disambiguationData":[OSD([sQuery(id+"F2.wireOp",EDGE,"E40.right")])],"isStart":true});
            var Q4;
            Q4=makeQuery(id+"F15.opExtrude","SWEPT_EDGE",EDGE,{"disambiguationData":[OSD([sQuery(id+"F2.wireOp",EDGE,"E40.top"),sQuery(id+"F2.wireOp",EDGE,"E40.right")])]});
            var Q5;
            Q5=makeQuery(id+"F15.opExtrude","SWEPT_EDGE",EDGE,{"disambiguationData":[OSD([sQuery(id+"F2.wireOp",EDGE,"E41.top"),sQuery(id+"F2.wireOp",EDGE,"E41.right")])]});
            var Q6;
            Q6=makeQuery(id+"F15.opExtrude","SWEPT_EDGE",EDGE,{"disambiguationData":[OSD([sQuery(id+"F2.wireOp",EDGE,"E41.bottom"),sQuery(id+"F2.wireOp",EDGE,"E41.right")])]});
            var Q7;
            Q7=makeQuery(id+"F15.opExtrude","SWEPT_EDGE",EDGE,{"disambiguationData":[OSD([sQuery(id+"F2.wireOp",EDGE,"E40.bottom"),sQuery(id+"F2.wireOp",EDGE,"E40.right")])]});
            fillet(context, id + "F20", {"entities" : qUnion([Q0, Q1, Q2, Q3, Q4, Q5, Q6, Q7]), "radius" : 1 * mm, "tangentPropagation" : true, "allowEdgeOverflow" : false});
        }
        {
            var Q0;
            Q0=makeQuery(id+"F17.opExtrude","CAP_EDGE",EDGE,{"disambiguationData":[OSD([sQuery(id+"F16.wireOp",EDGE,"E58.left")])],"isStart":false});
            var Q1;
            Q1=makeQuery(id+"F17.opExtrude","CAP_EDGE",EDGE,{"disambiguationData":[OSD([sQuery(id+"F16.wireOp",EDGE,"E58.bottom")])],"isStart":false});
            var Q2;
            Q2=makeQuery(id+"F17.opExtrude","CAP_EDGE",EDGE,{"disambiguationData":[OSD([sQuery(id+"F16.wireOp",EDGE,"E58.right")])],"isStart":false});
            var Q3;
            Q3=makeQuery(id+"F17.opExtrude","CAP_EDGE",EDGE,{"disambiguationData":[OSD([sQuery(id+"F16.wireOp",EDGE,"E58.top")])],"isStart":false});
            chamfer(context, id + "F21", {"entities" : qUnion([Q0, Q1, Q2, Q3]), "width" : 1 * mm, "tangentPropagation" : true});
        }
        {
            var Q0;
            Q0=makeQuery(id+"F1.opExtrude","CAP_FACE",FACE,{"disambiguationData":[OSD([sQuery(id+"F0.wireOp",EDGE,"E0.bottom"),sQuery(id+"F0.wireOp",EDGE,"E0.top"),sQuery(id+"F0.wireOp",EDGE,"E0.left"),sQuery(id+"F0.wireOp",EDGE,"E0.right"),sQuery(id+"F0.wireOp",EDGE,"E1"),sQuery(id+"F0.wireOp",EDGE,"E2"),sQuery(id+"F0.wireOp",EDGE,"E3"),sQuery(id+"F0.wireOp",EDGE,"E4.bottom"),sQuery(id+"F0.wireOp",EDGE,"E4.top"),sQuery(id+"F0.wireOp",EDGE,"E4.left"),sQuery(id+"F0.wireOp",EDGE,"E4.right"),sQuery(id+"F0.wireOp",EDGE,"E11.left"),sQuery(id+"F0.wireOp",EDGE,"E11.right")])],"isStart":false});
            var sketch = newSketch(context, id + "F22", { "sketchPlane" : qUnion([Q0])});
            skCircle(sketch, "E63", {"center": v(-20.5, 23) * mm, "radius": 1.5 * mm});
            skCircle(sketch, "E64", {"center": v(20.5, -23) * mm, "radius": 1.5 * mm});
            skCircle(sketch, "E65", {"center": v(-7.5, -18) * mm, "radius": 8.5 * mm, "construction": true});
            skLineSegment(sketch, "E66.bottom", {"start": v(-25.5, 28) * mm, "end": v(25.5, 28) * mm});
            skLineSegment(sketch, "E66.top", {"start": v(-25.5, -28) * mm, "end": v(25.5, -28) * mm});
            skLineSegment(sketch, "E66.left", {"start": v(-25.5, 28) * mm, "end": v(-25.5, -28) * mm});
            skLineSegment(sketch, "E66.right", {"start": v(25.5, 28) * mm, "end": v(25.5, -28) * mm});
            skLineSegment(sketch, "E67.bottom", {"start": v(-15.25, 11.75) * mm, "end": v(15.25, 11.75) * mm});
            skLineSegment(sketch, "E67.top", {"start": v(-15.25, -2.75) * mm, "end": v(15.25, -2.75) * mm});
            skLineSegment(sketch, "E67.left", {"start": v(-15.25, 11.75) * mm, "end": v(-15.25, -2.75) * mm});
            skLineSegment(sketch, "E67.right", {"start": v(15.25, 11.75) * mm, "end": v(15.25, -2.75) * mm});
            skCircle(sketch, "E68", {"center": v(-22.25, 4.75) * mm, "radius": 2 * mm, "construction": true});
            skCircle(sketch, "E69", {"center": v(22.25, 4.75) * mm, "radius": 2 * mm, "construction": true});
            skLineSegment(sketch, "E70.bottom", {"start": v(5, -27) * mm, "end": v(-20, -27) * mm});
            skLineSegment(sketch, "E70.top", {"start": v(5, -9) * mm, "end": v(-20, -9) * mm});
            skLineSegment(sketch, "E70.left", {"start": v(5, -27) * mm, "end": v(5, -9) * mm});
            skLineSegment(sketch, "E70.right", {"start": v(-20, -27) * mm, "end": v(-20, -9) * mm});
            skSolve(sketch);
        }
        {
            var Q0;
            Q0=makeQuery(id+"F11.opExtrude","CAP_FACE",FACE,{"disambiguationData":[OSD([sQuery(id+"F2.wireOp",EDGE,"E30.bottom"),sQuery(id+"F2.wireOp",EDGE,"E30.top"),sQuery(id+"F2.wireOp",EDGE,"E30.left"),sQuery(id+"F2.wireOp",EDGE,"E30.right"),sQuery(id+"F2.wireOp",EDGE,"E35.bottom"),sQuery(id+"F2.wireOp",EDGE,"E35.top"),sQuery(id+"F2.wireOp",EDGE,"E35.left"),sQuery(id+"F2.wireOp",EDGE,"E35.right"),sQuery(id+"F2.wireOp",EDGE,"E36.left"),sQuery(id+"F2.wireOp",EDGE,"E36.right"),sQuery(id+"F2.wireOp",EDGE,"E37.bottom"),sQuery(id+"F2.wireOp",EDGE,"E37.top")])],"isStart":false});
            var sketch = newSketch(context, id + "F23", { "sketchPlane" : qUnion([Q0])});
            skLineSegment(sketch, "E71.bottom", {"start": v(-63, -101.08) * mm, "end": v(-50.5, -101.08) * mm});
            skLineSegment(sketch, "E71.top", {"start": v(-63, -102.08) * mm, "end": v(-50.5, -102.08) * mm});
            skLineSegment(sketch, "E71.left", {"start": v(-63, -101.08) * mm, "end": v(-63, -102.08) * mm});
            skLineSegment(sketch, "E71.right", {"start": v(-50.5, -101.08) * mm, "end": v(-50.5, -102.08) * mm});
            skLineSegment(sketch, "E72.bottom", {"start": v(-63, -102.08) * mm, "end": v(-62, -102.08) * mm});
            skLineSegment(sketch, "E72.top", {"start": v(-63, -115.08) * mm, "end": v(-62, -115.08) * mm});
            skLineSegment(sketch, "E72.left", {"start": v(-63, -102.08) * mm, "end": v(-63, -115.08) * mm});
            skLineSegment(sketch, "E72.right", {"start": v(-62, -102.08) * mm, "end": v(-62, -115.08) * mm});
            skLineSegment(sketch, "E73.bottom", {"start": v(-50.5, -114.08) * mm, "end": v(-62, -114.08) * mm});
            skLineSegment(sketch, "E73.top", {"start": v(-50.5, -115.08) * mm, "end": v(-62, -115.08) * mm});
            skLineSegment(sketch, "E73.left", {"start": v(-50.5, -114.08) * mm, "end": v(-50.5, -115.08) * mm});
            skLineSegment(sketch, "E73.right", {"start": v(-62, -114.08) * mm, "end": v(-62, -115.08) * mm});
            skLineSegment(sketch, "E74.bottom", {"start": v(-33, -101.08) * mm, "end": v(-45.5, -101.08) * mm});
            skLineSegment(sketch, "E74.top", {"start": v(-33, -102.08) * mm, "end": v(-45.5, -102.08) * mm});
            skLineSegment(sketch, "E74.left", {"start": v(-33, -101.08) * mm, "end": v(-33, -102.08) * mm});
            skLineSegment(sketch, "E74.right", {"start": v(-45.5, -101.08) * mm, "end": v(-45.5, -102.08) * mm});
            skLineSegment(sketch, "E75.bottom", {"start": v(-33, -102.08) * mm, "end": v(-34, -102.08) * mm});
            skLineSegment(sketch, "E75.top", {"start": v(-33, -115.08) * mm, "end": v(-34, -115.08) * mm});
            skLineSegment(sketch, "E75.left", {"start": v(-33, -102.08) * mm, "end": v(-33, -115.08) * mm});
            skLineSegment(sketch, "E75.right", {"start": v(-34, -102.08) * mm, "end": v(-34, -115.08) * mm});
            skLineSegment(sketch, "E76.bottom", {"start": v(-45.5, -114.08) * mm, "end": v(-34, -114.08) * mm});
            skLineSegment(sketch, "E76.top", {"start": v(-45.5, -115.08) * mm, "end": v(-34, -115.08) * mm});
            skLineSegment(sketch, "E76.left", {"start": v(-45.5, -114.08) * mm, "end": v(-45.5, -115.08) * mm});
            skLineSegment(sketch, "E76.right", {"start": v(-34, -114.08) * mm, "end": v(-34, -115.08) * mm});
            skSolve(sketch);
        }
        {
            var Q0;
            {var subQ0=sQuery(id+"F0.wireOp",EDGE,"E3");Q0=makeQuery(id+"FKRJtqk0ZjomfcX_7.boolean.opBoolean","SPLIT",FACE,{"disambiguationData":[TD([makeQuery(id+"F1.opExtrude","SWEPT_FACE",FACE,{"disambiguationData":[OSD([subQ0])]})])],"derivedFrom":makeQuery(id+"F1.opExtrude","CAP_FACE",FACE,{"disambiguationData":[OSD([sQuery(id+"F0.wireOp",EDGE,"E0.bottom"),sQuery(id+"F0.wireOp",EDGE,"E0.top"),sQuery(id+"F0.wireOp",EDGE,"E0.left"),sQuery(id+"F0.wireOp",EDGE,"E0.right"),sQuery(id+"F0.wireOp",EDGE,"E1"),sQuery(id+"F0.wireOp",EDGE,"E2"),subQ0,sQuery(id+"F0.wireOp",EDGE,"E4.bottom"),sQuery(id+"F0.wireOp",EDGE,"E4.top"),sQuery(id+"F0.wireOp",EDGE,"E4.left"),sQuery(id+"F0.wireOp",EDGE,"E4.right"),sQuery(id+"F0.wireOp",EDGE,"E11.left"),sQuery(id+"F0.wireOp",EDGE,"E11.right")])],"isStart":false})});}
            extrude(context, id + "F24", {"entities" : qUnion([Q0]), "operationType" : NewBodyOperationType.ADD, "depth" : 1 * mm});
        }
        {
            var Q0;
            Q0=sQuery(id+"F22.wireOp",VERTEX,"E68.center");
            var Q1;
            Q1=sQuery(id+"F22.wireOp",VERTEX,"E69.center");
            var Q2;
            Q2=makeQuery(id+"F1.opExtrude","SWEPT_BODY",BODY,{"disambiguationData":[OSD([sQuery(id+"F0.wireOp",EDGE,"E0.bottom"),sQuery(id+"F0.wireOp",EDGE,"E0.top"),sQuery(id+"F0.wireOp",EDGE,"E0.left"),sQuery(id+"F0.wireOp",EDGE,"E0.right"),sQuery(id+"F0.wireOp",EDGE,"E1"),sQuery(id+"F0.wireOp",EDGE,"E2"),sQuery(id+"F0.wireOp",EDGE,"E3"),sQuery(id+"F0.wireOp",EDGE,"E4.bottom"),sQuery(id+"F0.wireOp",EDGE,"E4.top"),sQuery(id+"F0.wireOp",EDGE,"E4.left"),sQuery(id+"F0.wireOp",EDGE,"E4.right"),sQuery(id+"F0.wireOp",EDGE,"E11.left"),sQuery(id+"F0.wireOp",EDGE,"E11.right")])]});
            hole(context, id + "F25", {"style" : HoleStyle.SIMPLE, "endStyle" : HoleEndStyle.THROUGH, "holeDiameter" : 1.4 * mm, "isTappedThrough" : true, "tappedDepth" : 12 * mm, "tapClearance" : 3, "locations" : qUnion([Q0, Q1]), "scope" : qUnion([Q2])});
        }
        {
            var Q0;
            {var subQ0=sQuery(id+"F2.wireOp",EDGE,"E37.top");var subQ1=sQuery(id+"F2.wireOp",EDGE,"E37.bottom");var subQ2=sQuery(id+"F2.wireOp",EDGE,"E36.right");var subQ3=sQuery(id+"F2.wireOp",EDGE,"E36.left");Q0=makeQuery(id+"F13.boolean.opBoolean","MERGE",FACE,{"derivedFrom":[makeQuery(id+"F11.opExtrude","CAP_FACE",FACE,{"disambiguationData":[OSD([sQuery(id+"F2.wireOp",EDGE,"E30.bottom"),sQuery(id+"F2.wireOp",EDGE,"E30.top"),sQuery(id+"F2.wireOp",EDGE,"E30.left"),sQuery(id+"F2.wireOp",EDGE,"E30.right"),sQuery(id+"F2.wireOp",EDGE,"E35.bottom"),sQuery(id+"F2.wireOp",EDGE,"E35.top"),sQuery(id+"F2.wireOp",EDGE,"E35.left"),sQuery(id+"F2.wireOp",EDGE,"E35.right"),subQ3,subQ2,subQ1,subQ0])],"isStart":true}),makeQuery(id+"F13.opExtrude","CAP_FACE",FACE,{"disambiguationData":[OSD([sQuery(id+"F2.wireOp",EDGE,"E36.bottom"),sQuery(id+"F2.wireOp",EDGE,"E36.top"),subQ3,subQ2,subQ1,subQ0,sQuery(id+"F2.wireOp",EDGE,"E37.left"),sQuery(id+"F2.wireOp",EDGE,"E37.right")])],"isStart":true})]});}
            var sketch = newSketch(context, id + "F26", { "sketchPlane" : qUnion([Q0])});
            skLineSegment(sketch, "E77.bottom", {"start": v(-63, 115.08) * mm, "end": v(-33, 115.08) * mm});
            skLineSegment(sketch, "E77.top", {"start": v(-63, 114.08) * mm, "end": v(-33, 114.08) * mm});
            skLineSegment(sketch, "E77.left", {"start": v(-63, 115.08) * mm, "end": v(-63, 114.08) * mm});
            skLineSegment(sketch, "E77.right", {"start": v(-33, 115.08) * mm, "end": v(-33, 114.08) * mm});
            skLineSegment(sketch, "E78.bottom", {"start": v(-63, 114.08) * mm, "end": v(-62, 114.08) * mm});
            skLineSegment(sketch, "E78.top", {"start": v(-63, 101.08) * mm, "end": v(-62, 101.08) * mm});
            skLineSegment(sketch, "E78.left", {"start": v(-63, 114.08) * mm, "end": v(-63, 101.08) * mm});
            skLineSegment(sketch, "E78.right", {"start": v(-62, 114.08) * mm, "end": v(-62, 101.08) * mm});
            skLineSegment(sketch, "E79.bottom", {"start": v(-62, 101.08) * mm, "end": v(-33, 101.08) * mm});
            skLineSegment(sketch, "E79.top", {"start": v(-62, 102.08) * mm, "end": v(-33, 102.08) * mm});
            skLineSegment(sketch, "E79.left", {"start": v(-62, 101.08) * mm, "end": v(-62, 102.08) * mm});
            skLineSegment(sketch, "E79.right", {"start": v(-33, 101.08) * mm, "end": v(-33, 102.08) * mm});
            skLineSegment(sketch, "E80.bottom", {"start": v(-33, 114.08) * mm, "end": v(-34, 114.08) * mm});
            skLineSegment(sketch, "E80.top", {"start": v(-33, 102.08) * mm, "end": v(-34, 102.08) * mm});
            skLineSegment(sketch, "E80.left", {"start": v(-33, 114.08) * mm, "end": v(-33, 102.08) * mm});
            skLineSegment(sketch, "E80.right", {"start": v(-34, 114.08) * mm, "end": v(-34, 102.08) * mm});
            skSolve(sketch);
        }
        {
            var Q0;
            Q0=sQuery(id+"F22.wireOp",VERTEX,"E68.center");
            var Q1;
            Q1=sQuery(id+"F22.wireOp",VERTEX,"E69.center");
            var Q2;
            Q2=makeQuery(id+"F1.opExtrude","SWEPT_BODY",BODY,{"disambiguationData":[OSD([sQuery(id+"F0.wireOp",EDGE,"E0.bottom"),sQuery(id+"F0.wireOp",EDGE,"E0.top"),sQuery(id+"F0.wireOp",EDGE,"E0.left"),sQuery(id+"F0.wireOp",EDGE,"E0.right"),sQuery(id+"F0.wireOp",EDGE,"E1"),sQuery(id+"F0.wireOp",EDGE,"E2"),sQuery(id+"F0.wireOp",EDGE,"E3"),sQuery(id+"F0.wireOp",EDGE,"E4.bottom"),sQuery(id+"F0.wireOp",EDGE,"E4.top"),sQuery(id+"F0.wireOp",EDGE,"E4.left"),sQuery(id+"F0.wireOp",EDGE,"E4.right"),sQuery(id+"F0.wireOp",EDGE,"E11.left"),sQuery(id+"F0.wireOp",EDGE,"E11.right")])]});
            hole(context, id + "F27", {"style" : HoleStyle.SIMPLE, "endStyle" : HoleEndStyle.THROUGH, "oppositeDirection" : true, "holeDiameter" : 1.4 * mm, "isTappedThrough" : true, "tappedDepth" : 12 * mm, "tapClearance" : 3, "locations" : qUnion([Q0, Q1]), "scope" : qUnion([Q2])});
        }
        {
            var Q0;
            Q0=makeQuery(id+"F22.imprint","IMPRINT",FACE,{"disambiguationData":[TD([[makeQuery(id+"F22.imprint","IMPRINT",EDGE,{"derivedFrom":sQuery(id+"F22.wireOp",EDGE,"E63")}),-1.0]])]});
            extrude(context, id + "F28", {"entities" : qUnion([Q0]), "operationType" : NewBodyOperationType.ADD, "depth" : 5 * mm});
        }
        {
            var Q0;
            Q0=makeQuery(id+"F1.opExtrude","CAP_FACE",FACE,{"disambiguationData":[OSD([sQuery(id+"F0.wireOp",EDGE,"E0.bottom"),sQuery(id+"F0.wireOp",EDGE,"E0.top"),sQuery(id+"F0.wireOp",EDGE,"E0.left"),sQuery(id+"F0.wireOp",EDGE,"E0.right"),sQuery(id+"F0.wireOp",EDGE,"E1"),sQuery(id+"F0.wireOp",EDGE,"E2"),sQuery(id+"F0.wireOp",EDGE,"E3"),sQuery(id+"F0.wireOp",EDGE,"E4.bottom"),sQuery(id+"F0.wireOp",EDGE,"E4.top"),sQuery(id+"F0.wireOp",EDGE,"E4.left"),sQuery(id+"F0.wireOp",EDGE,"E4.right"),sQuery(id+"F0.wireOp",EDGE,"E11.left"),sQuery(id+"F0.wireOp",EDGE,"E11.right")])],"isStart":true});
            var sketch = newSketch(context, id + "F29", { "sketchPlane" : qUnion([Q0])});
            skLineSegment(sketch, "E81.bottom", {"start": v(-25.5, 28) * mm, "end": v(25.5, 28) * mm});
            skLineSegment(sketch, "E81.top", {"start": v(-25.5, 27.8) * mm, "end": v(25.5, 27.8) * mm});
            skLineSegment(sketch, "E81.left", {"start": v(-25.5, 28) * mm, "end": v(-25.5, 27.8) * mm});
            skLineSegment(sketch, "E81.right", {"start": v(25.5, 28) * mm, "end": v(25.5, 27.8) * mm});
            skLineSegment(sketch, "E82.bottom", {"start": v(-25.5, -28) * mm, "end": v(25.5, -28) * mm});
            skLineSegment(sketch, "E82.top", {"start": v(-25.5, -27.8) * mm, "end": v(25.5, -27.8) * mm});
            skLineSegment(sketch, "E82.left", {"start": v(-25.5, -28) * mm, "end": v(-25.5, -27.8) * mm});
            skLineSegment(sketch, "E82.right", {"start": v(25.5, -28) * mm, "end": v(25.5, -27.8) * mm});
            skLineSegment(sketch, "E83.bottom", {"start": v(-25.5, -27.8) * mm, "end": v(-25.3, -27.8) * mm});
            skLineSegment(sketch, "E83.top", {"start": v(-25.5, 27.8) * mm, "end": v(-25.3, 27.8) * mm});
            skLineSegment(sketch, "E83.left", {"start": v(-25.5, -27.8) * mm, "end": v(-25.5, 27.8) * mm});
            skLineSegment(sketch, "E83.right", {"start": v(-25.3, -27.8) * mm, "end": v(-25.3, 27.8) * mm});
            skLineSegment(sketch, "E84.bottom", {"start": v(25.5, -27.8) * mm, "end": v(25.3, -27.8) * mm});
            skLineSegment(sketch, "E84.top", {"start": v(25.5, 27.8) * mm, "end": v(25.3, 27.8) * mm});
            skLineSegment(sketch, "E84.left", {"start": v(25.5, -27.8) * mm, "end": v(25.5, 27.8) * mm});
            skLineSegment(sketch, "E84.right", {"start": v(25.3, -27.8) * mm, "end": v(25.3, 27.8) * mm});
            skSolve(sketch);
        }
        {
            var Q0;
            Q0=qSketchRegion(id+"F29",true);
            extrude(context, id + "F30", {"entities" : qUnion([Q0]), "operationType" : NewBodyOperationType.REMOVE, "oppositeDirection" : true, "depth" : 25 * mm});
        }
        {
            var Q0;
            Q0=sQuery(id+"F22.wireOp",VERTEX,"E68.center");
            var Q1;
            Q1=sQuery(id+"F22.wireOp",VERTEX,"E69.center");
            var Q2;
            Q2=makeQuery(id+"F1.opExtrude","SWEPT_BODY",BODY,{"disambiguationData":[OSD([sQuery(id+"F0.wireOp",EDGE,"E0.bottom"),sQuery(id+"F0.wireOp",EDGE,"E0.top"),sQuery(id+"F0.wireOp",EDGE,"E0.left"),sQuery(id+"F0.wireOp",EDGE,"E0.right"),sQuery(id+"F0.wireOp",EDGE,"E1"),sQuery(id+"F0.wireOp",EDGE,"E2"),sQuery(id+"F0.wireOp",EDGE,"E3"),sQuery(id+"F0.wireOp",EDGE,"E4.bottom"),sQuery(id+"F0.wireOp",EDGE,"E4.top"),sQuery(id+"F0.wireOp",EDGE,"E4.left"),sQuery(id+"F0.wireOp",EDGE,"E4.right"),sQuery(id+"F0.wireOp",EDGE,"E11.left"),sQuery(id+"F0.wireOp",EDGE,"E11.right")])]});
            hole(context, id + "F31", {"style" : HoleStyle.SIMPLE, "endStyle" : HoleEndStyle.THROUGH, "oppositeDirection" : true, "holeDiameter" : 1.6 * mm, "isTappedThrough" : true, "tappedDepth" : 12 * mm, "tapClearance" : 3, "locations" : qUnion([Q0, Q1]), "scope" : qUnion([Q2])});
        }
        {
            var Q0;
            Q0=sQuery(id+"F22.wireOp",VERTEX,"E69.center");
            var Q1;
            Q1=sQuery(id+"F22.wireOp",VERTEX,"E68.center");
            var Q2;
            Q2=makeQuery(id+"F1.opExtrude","SWEPT_BODY",BODY,{"disambiguationData":[OSD([sQuery(id+"F0.wireOp",EDGE,"E0.bottom"),sQuery(id+"F0.wireOp",EDGE,"E0.top"),sQuery(id+"F0.wireOp",EDGE,"E0.left"),sQuery(id+"F0.wireOp",EDGE,"E0.right"),sQuery(id+"F0.wireOp",EDGE,"E1"),sQuery(id+"F0.wireOp",EDGE,"E2"),sQuery(id+"F0.wireOp",EDGE,"E3"),sQuery(id+"F0.wireOp",EDGE,"E4.bottom"),sQuery(id+"F0.wireOp",EDGE,"E4.top"),sQuery(id+"F0.wireOp",EDGE,"E4.left"),sQuery(id+"F0.wireOp",EDGE,"E4.right"),sQuery(id+"F0.wireOp",EDGE,"E11.left"),sQuery(id+"F0.wireOp",EDGE,"E11.right")])]});
            hole(context, id + "F32", {"style" : HoleStyle.SIMPLE, "endStyle" : HoleEndStyle.THROUGH, "holeDiameter" : 1.6 * mm, "isTappedThrough" : true, "tappedDepth" : 12 * mm, "tapClearance" : 3, "locations" : qUnion([Q0, Q1]), "scope" : qUnion([Q2])});
        }
        {
            var Q0;
            Q0=makeQuery(id+"F1.opExtrude","CAP_FACE",FACE,{"disambiguationData":[OSD([sQuery(id+"F0.wireOp",EDGE,"E0.bottom"),sQuery(id+"F0.wireOp",EDGE,"E0.top"),sQuery(id+"F0.wireOp",EDGE,"E0.left"),sQuery(id+"F0.wireOp",EDGE,"E0.right"),sQuery(id+"F0.wireOp",EDGE,"E1"),sQuery(id+"F0.wireOp",EDGE,"E2"),sQuery(id+"F0.wireOp",EDGE,"E3"),sQuery(id+"F0.wireOp",EDGE,"E4.bottom"),sQuery(id+"F0.wireOp",EDGE,"E4.top"),sQuery(id+"F0.wireOp",EDGE,"E4.left"),sQuery(id+"F0.wireOp",EDGE,"E4.right"),sQuery(id+"F0.wireOp",EDGE,"E11.left"),sQuery(id+"F0.wireOp",EDGE,"E11.right")])],"isStart":true});
            var sketch = newSketch(context, id + "F33", { "sketchPlane" : qUnion([Q0])});
            skLineSegment(sketch, "E85.bottom", {"start": v(-9.88, -11.75) * mm, "end": v(-7.88, -11.75) * mm});
            skLineSegment(sketch, "E85.top", {"start": v(-9.88, 2.75) * mm, "end": v(-7.88, 2.75) * mm});
            skLineSegment(sketch, "E85.left", {"start": v(-9.88, -11.75) * mm, "end": v(-9.88, 2.75) * mm});
            skLineSegment(sketch, "E85.right", {"start": v(-7.88, -11.75) * mm, "end": v(-7.88, 2.75) * mm});
            skLineSegment(sketch, "E86.bottom", {"start": v(9.87, 2.75) * mm, "end": v(7.87, 2.75) * mm});
            skLineSegment(sketch, "E86.top", {"start": v(9.88, -11.75) * mm, "end": v(7.88, -11.75) * mm});
            skLineSegment(sketch, "E86.left", {"start": v(9.87, 2.75) * mm, "end": v(9.88, -11.75) * mm});
            skLineSegment(sketch, "E86.right", {"start": v(7.87, 2.75) * mm, "end": v(7.88, -11.75) * mm});
            skSolve(sketch);
        }
        {
            var Q0;
            Q0=makeQuery(id+"F33.imprint","IMPRINT",FACE,{"disambiguationData":[TD([[makeQuery(id+"F33.imprint","IMPRINT",EDGE,{"derivedFrom":sQuery(id+"F33.wireOp",EDGE,"E85.bottom")}),1.0]])]});
            var Q1;
            Q1=makeQuery(id+"F33.imprint","IMPRINT",FACE,{"disambiguationData":[TD([[makeQuery(id+"F33.imprint","IMPRINT",EDGE,{"derivedFrom":sQuery(id+"F33.wireOp",EDGE,"E86.bottom")}),-1.0]])]});
            extrude(context, id + "F34", {"entities" : qUnion([Q0, Q1]), "operationType" : NewBodyOperationType.ADD, "oppositeDirection" : true, "depth" : 2 * mm});
        }
    });
